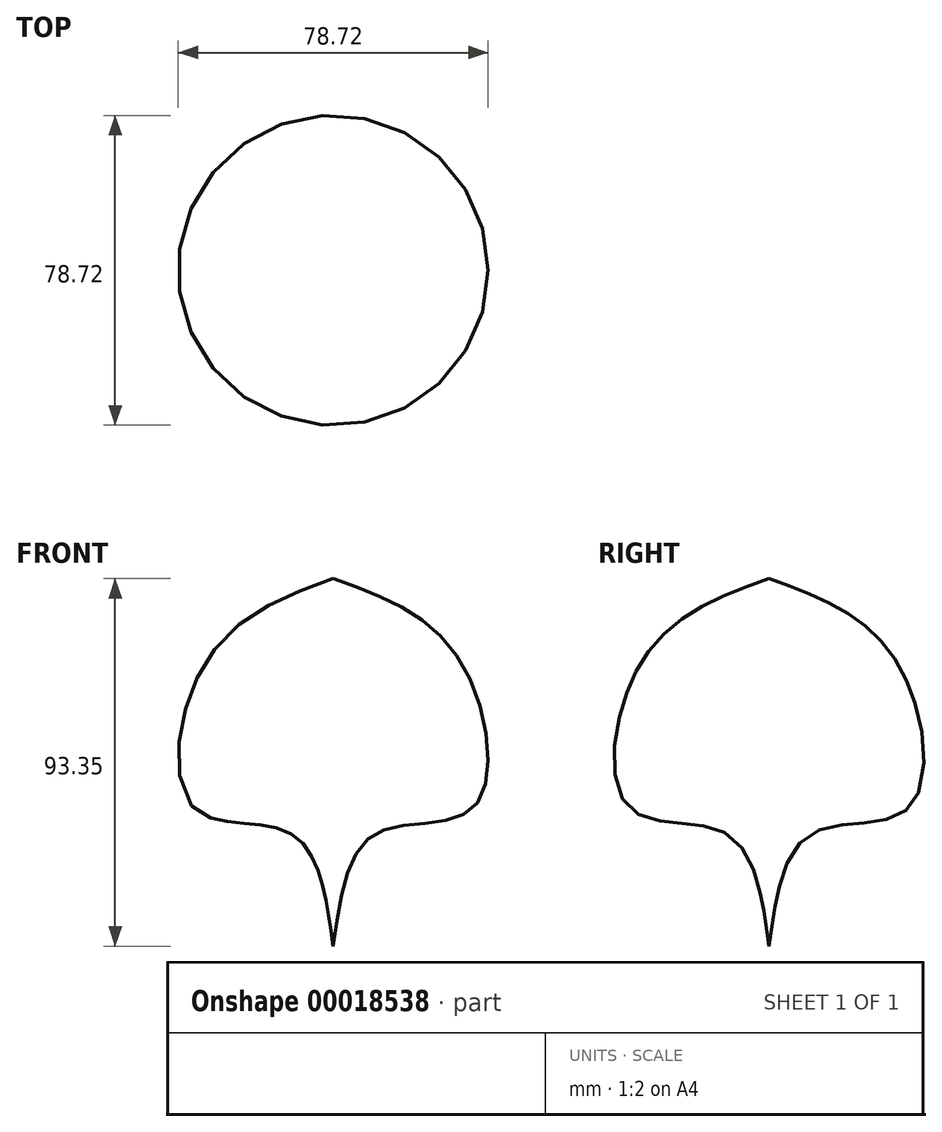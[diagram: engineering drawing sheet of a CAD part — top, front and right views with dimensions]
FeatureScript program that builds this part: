
annotation { "Feature Type Name" : "Feature", "Feature Type Description" : "" }
export const myFeature = defineFeature(function(context is Context, id is Id, definition is map)
    precondition{}
    {
        {
            var Q0;
            Q0=qCreatedBy(makeId("Front.planeOp"),FACE);
            var sketch = newSketch(context, id + "F0", { "sketchPlane" : qUnion([Q0])});
            skLineSegment(sketch, "E0", {"start": v(0, 47.4) * mm, "end": v(0, -45.96) * mm});
            skFitSpline(sketch, "E1", {"points": [v(0, 47.4) * mm, v(32.12, 26.73) * mm, v(35.44, -10.9) * mm, v(11.1, -17.18) * mm, v(0, -45.96) * mm], "startDerivative": vector(136.89, -48.9) * mm, "endDerivative": vector(-20.96, -152.3) * mm});
            skSolve(sketch);
        }
        {
            var Q0;
            Q0=sQuery(id+"F0.wireOp",EDGE,"E1");
            var Q1;
            Q1=sQuery(id+"F0.wireOp",EDGE,"E0");
            revolve(context, id + "F1", {"bodyType" : ToolBodyType.SURFACE, "surfaceOperationType" : NewSurfaceOperationType.NEW, "surfaceEntities" : qUnion([Q0]), "axis" : qUnion([Q1]), "revolveType" : RevolveType.FULL});
        }
    });
